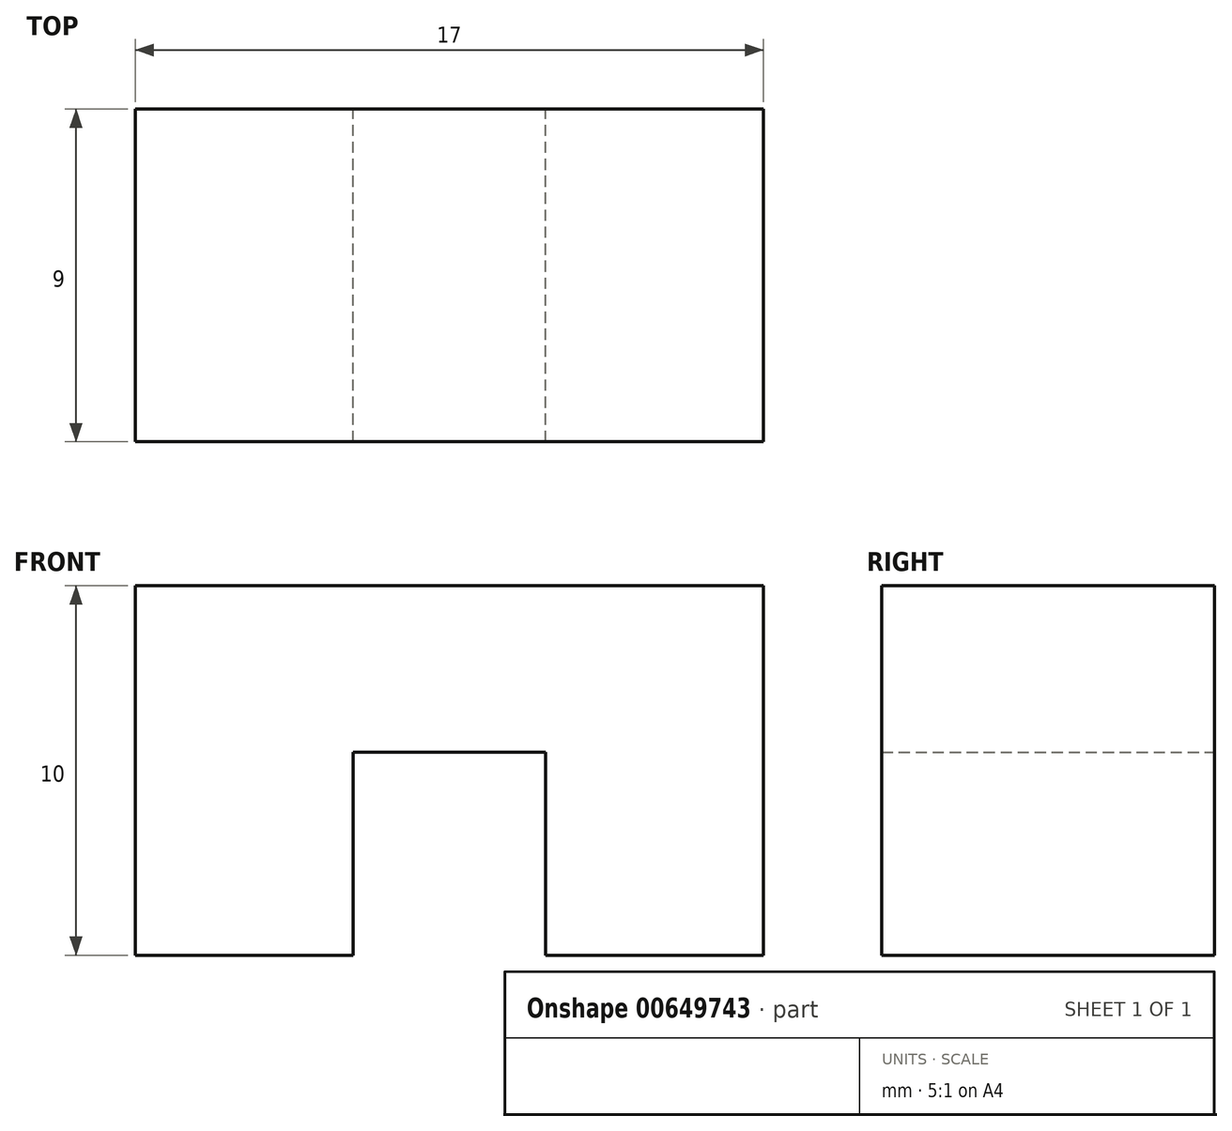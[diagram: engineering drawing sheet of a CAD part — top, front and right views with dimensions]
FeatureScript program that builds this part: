
annotation { "Feature Type Name" : "Feature", "Feature Type Description" : "" }
export const myFeature = defineFeature(function(context is Context, id is Id, definition is map)
    precondition{}
    {
        {
            var Q0;
            Q0=qCreatedBy(makeId("Front.planeOp"),FACE);
            var sketch = newSketch(context, id + "F0", { "sketchPlane" : qUnion([Q0])});
            skLineSegment(sketch, "E0", {"start": v(0, 10) * mm, "end": v(-8.5, 10) * mm});
            skLineSegment(sketch, "E1", {"start": v(-8.5, 10) * mm, "end": v(-8.5, 0) * mm});
            skLineSegment(sketch, "E2", {"start": v(-8.5, 0) * mm, "end": v(-2.6, 0) * mm});
            skLineSegment(sketch, "E3", {"start": v(-2.6, 0) * mm, "end": v(-2.6, 5.5) * mm});
            skLineSegment(sketch, "E4", {"start": v(-2.6, 5.5) * mm, "end": v(0, 5.5) * mm});
            skLineSegment(sketch, "E5.MirrorCS", {"start": v(8.5, 10) * mm, "end": v(8.5, 0) * mm});
            skLineSegment(sketch, "E6.MirrorCS", {"start": v(2.6, 0) * mm, "end": v(2.6, 5.5) * mm});
            skLineSegment(sketch, "E7.MirrorCS", {"start": v(2.6, 5.5) * mm, "end": v(0, 5.5) * mm});
            skLineSegment(sketch, "E8.MirrorCS", {"start": v(8.5, 0) * mm, "end": v(2.6, 0) * mm});
            skLineSegment(sketch, "E9.MirrorCS", {"start": v(0, 10) * mm, "end": v(8.5, 10) * mm});
            skSolve(sketch);
        }
        {
            var Q0;
            Q0=makeQuery(id+"F0.imprint","IMPRINT",FACE,{"disambiguationData":[TD([[makeQuery(id+"F0.imprint","IMPRINT",EDGE,{"derivedFrom":sQuery(id+"F0.wireOp",EDGE,"E0")}),1.0]])]});
            extrude(context, id + "F1", {"entities" : qUnion([Q0]), "depth" : 9 * mm, "offsetDistance" : 25.4 * mm});
        }
    });
